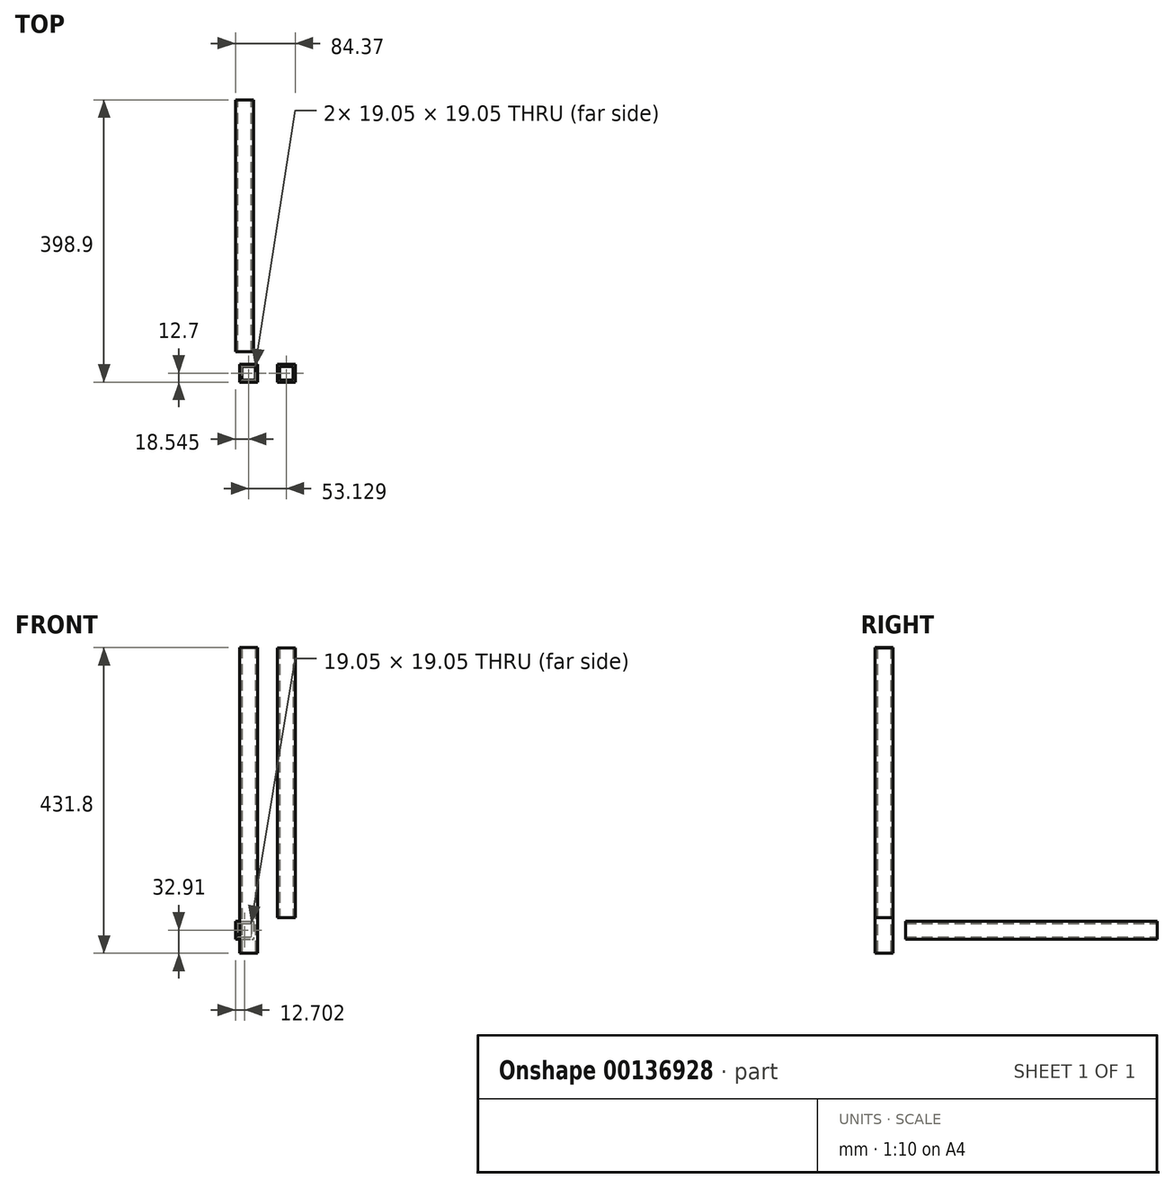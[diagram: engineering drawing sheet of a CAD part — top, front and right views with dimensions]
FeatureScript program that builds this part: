
annotation { "Feature Type Name" : "Feature", "Feature Type Description" : "" }
export const myFeature = defineFeature(function(context is Context, id is Id, definition is map)
    precondition{}
    {
        {
            var Q0;
            Q0=qCreatedBy(makeId("Front.planeOp"),FACE);
            var sketch = newSketch(context, id + "F0", { "sketchPlane" : qUnion([Q0])});
            skLineSegment(sketch, "E0.bottom", {"start": v(-31.27, 411.59) * mm, "end": v(-5.87, 411.59) * mm});
            skLineSegment(sketch, "E0.top", {"start": v(-31.27, -20.21) * mm, "end": v(-5.87, -20.21) * mm});
            skLineSegment(sketch, "E0.left", {"start": v(-31.27, 411.59) * mm, "end": v(-31.27, -20.21) * mm});
            skLineSegment(sketch, "E0.right", {"start": v(-5.87, 411.59) * mm, "end": v(-5.87, -20.21) * mm});
            skLineSegment(sketch, "E1.bottom", {"start": v(21.86, 411.06) * mm, "end": v(47.26, 411.06) * mm});
            skLineSegment(sketch, "E1.top", {"start": v(21.86, 30.06) * mm, "end": v(47.26, 30.06) * mm});
            skLineSegment(sketch, "E1.left", {"start": v(21.86, 411.06) * mm, "end": v(21.86, 30.06) * mm});
            skLineSegment(sketch, "E1.right", {"start": v(47.26, 411.06) * mm, "end": v(47.26, 30.06) * mm});
            skSolve(sketch);
        }
        {
            var Q0;
            Q0 = qSketchRegion(id + "F0", true);
            extrude(context, id + "F1", {"entities" : qUnion([Q0]), "depth" : 25.4 * mm});
        }
        {
            var Q0;
            Q0=makeQuery(id+"F1.opExtrude","SWEPT_FACE",FACE,{"disambiguationData":[OSD([sQuery(id+"F0.wireOp",EDGE,"E0.bottom")])]});
            var Q1;
            Q1=makeQuery(id+"F1.opExtrude","SWEPT_FACE",FACE,{"disambiguationData":[OSD([sQuery(id+"F0.wireOp",EDGE,"E1.bottom")])]});
            var Q2;
            Q2=makeQuery(id+"F1.opExtrude","SWEPT_FACE",FACE,{"disambiguationData":[OSD([sQuery(id+"F0.wireOp",EDGE,"E1.top")])]});
            var Q3;
            Q3=makeQuery(id+"F1.opExtrude","SWEPT_FACE",FACE,{"disambiguationData":[OSD([sQuery(id+"F0.wireOp",EDGE,"E0.top")])]});
            shell(context, id + "F2", {"entities" : qUnion([Q0, Q1, Q2, Q3]), "thickness" : 3.17 * mm});
        }
        {
            var Q0;
            Q0=qCreatedBy(makeId("Top.planeOp"),FACE);
            var sketch = newSketch(context, id + "F3", { "sketchPlane" : qUnion([Q0])});
            skLineSegment(sketch, "E2.bottom", {"start": v(-37.1, 17.9) * mm, "end": v(-11.7, 17.9) * mm});
            skLineSegment(sketch, "E2.top", {"start": v(-37.1, 373.5) * mm, "end": v(-11.7, 373.5) * mm});
            skLineSegment(sketch, "E2.left", {"start": v(-37.1, 17.9) * mm, "end": v(-37.1, 373.5) * mm});
            skLineSegment(sketch, "E2.right", {"start": v(-11.7, 17.9) * mm, "end": v(-11.7, 373.5) * mm});
            skSolve(sketch);
        }
        {
            var Q0;
            Q0 = qSketchRegion(id + "F3", true);
            extrude(context, id + "F4", {"entities" : qUnion([Q0]), "depth" : 25.4 * mm});
        }
        {
            var Q0;
            Q0=makeQuery(id+"F4.opExtrude","SWEPT_FACE",FACE,{"disambiguationData":[OSD([sQuery(id+"F3.wireOp",EDGE,"E2.top")])]});
            var Q1;
            Q1=makeQuery(id+"F4.opExtrude","SWEPT_FACE",FACE,{"disambiguationData":[OSD([sQuery(id+"F3.wireOp",EDGE,"E2.bottom")])]});
            shell(context, id + "F5", {"entities" : qUnion([Q0, Q1]), "thickness" : 3.17 * mm});
        }
    });
